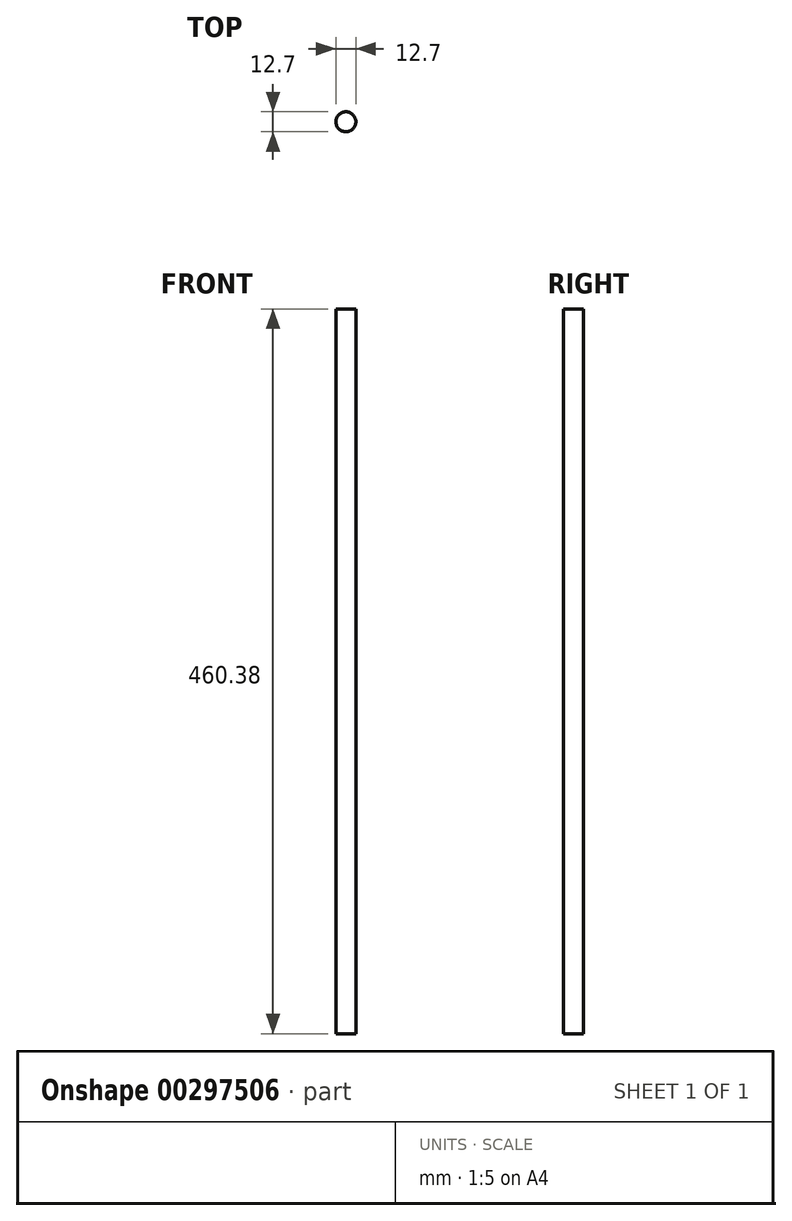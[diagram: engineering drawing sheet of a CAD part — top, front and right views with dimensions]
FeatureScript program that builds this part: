
annotation { "Feature Type Name" : "Feature", "Feature Type Description" : "" }
export const myFeature = defineFeature(function(context is Context, id is Id, definition is map)
    precondition{}
    {
        {
            var Q0;
            Q0=qCreatedBy(makeId("Front.planeOp"),FACE);
            var sketch = newSketch(context, id + "F0", { "sketchPlane" : qUnion([Q0])});
            skCircle(sketch, "E0", {"center": v(0, 0) * mm, "radius": 230.19 * mm});
            skLineSegment(sketch, "E1", {"start": v(0, 230.19) * mm, "end": v(0, -230.19) * mm});
            skLineSegment(sketch, "E2", {"start": v(-230.19, 0) * mm, "end": v(230.19, 0) * mm});
            skLineSegment(sketch, "E3", {"start": v(0, 0) * mm, "end": v(-76.2, 0) * mm});
            skLineSegment(sketch, "E4", {"start": v(0, 0) * mm, "end": v(0, 76.2) * mm});
            skLineSegment(sketch, "E5", {"start": v(0, 0) * mm, "end": v(76.2, 0) * mm});
            skLineSegment(sketch, "E6", {"start": v(0, 0) * mm, "end": v(0, -76.2) * mm});
            skLineSegment(sketch, "E7", {"start": v(0, 76.2) * mm, "end": v(0, 152.4) * mm});
            skLineSegment(sketch, "E8", {"start": v(76.2, 0) * mm, "end": v(152.4, 0) * mm});
            skLineSegment(sketch, "E9", {"start": v(-76.2, 0) * mm, "end": v(-152.4, 0) * mm});
            skLineSegment(sketch, "E10", {"start": v(0, -76.2) * mm, "end": v(0, -152.4) * mm});
            skLineSegment(sketch, "E11", {"start": v(-76.2, 217.2) * mm, "end": v(-76.2, -217.2) * mm});
            skLineSegment(sketch, "E12", {"start": v(-152.4, 172.51) * mm, "end": v(-152.4, -172.51) * mm});
            skLineSegment(sketch, "E13", {"start": v(76.2, 0) * mm, "end": v(76.2, 217.2) * mm});
            skLineSegment(sketch, "E14", {"start": v(76.2, 0) * mm, "end": v(76.2, -217.2) * mm});
            skLineSegment(sketch, "E15", {"start": v(152.4, 172.51) * mm, "end": v(152.4, -172.51) * mm});
            skLineSegment(sketch, "E16", {"start": v(217.2, 76.2) * mm, "end": v(-217.2, 76.2) * mm});
            skLineSegment(sketch, "E17", {"start": v(172.51, 152.4) * mm, "end": v(-172.51, 152.4) * mm});
            skLineSegment(sketch, "E18", {"start": v(217.2, -76.2) * mm, "end": v(-217.2, -76.2) * mm});
            skLineSegment(sketch, "E19", {"start": v(172.51, -152.4) * mm, "end": v(-172.51, -152.4) * mm});
            skLineSegment(sketch, "E20", {"start": v(0, 230.19) * mm, "end": v(80.44, 230.19) * mm});
            skSolve(sketch);
        }
        {
            var Q0;
            Q0=sQuery(id+"F0.wireOp",EDGE,"E20");
            cPlane(context, id + "F1", {"entities" : qUnion([Q0]), "cplaneType" : CPlaneType.LINE_ANGLE, "offset" : 25.4 * mm, "angle" : 90 * degree, "width" : 152.4 * mm, "height" : 152.4 * mm});
        }
        {
            var Q0;
            Q0=qCreatedBy(id+"F1.planeOp",FACE);
            var sketch = newSketch(context, id + "F2", { "sketchPlane" : qUnion([Q0])});
            skCircle(sketch, "E21", {"center": v(0, 0) * mm, "radius": 6.35 * mm});
            skSolve(sketch);
        }
        {
            var Q0;
            Q0=makeQuery(id+"F2.imprint","IMPRINT",FACE,{"disambiguationData":[TD([[makeQuery(id+"F2.imprint","IMPRINT",EDGE,{"derivedFrom":sQuery(id+"F2.wireOp",EDGE,"E21")}),1.0]])]});
            var Q1;
            Q1=sQuery(id+"F0.wireOp",EDGE,"E1");
            sweep(context, id + "F3", {"profiles" : qUnion([Q0]), "path" : qUnion([Q1])});
        }
    });
